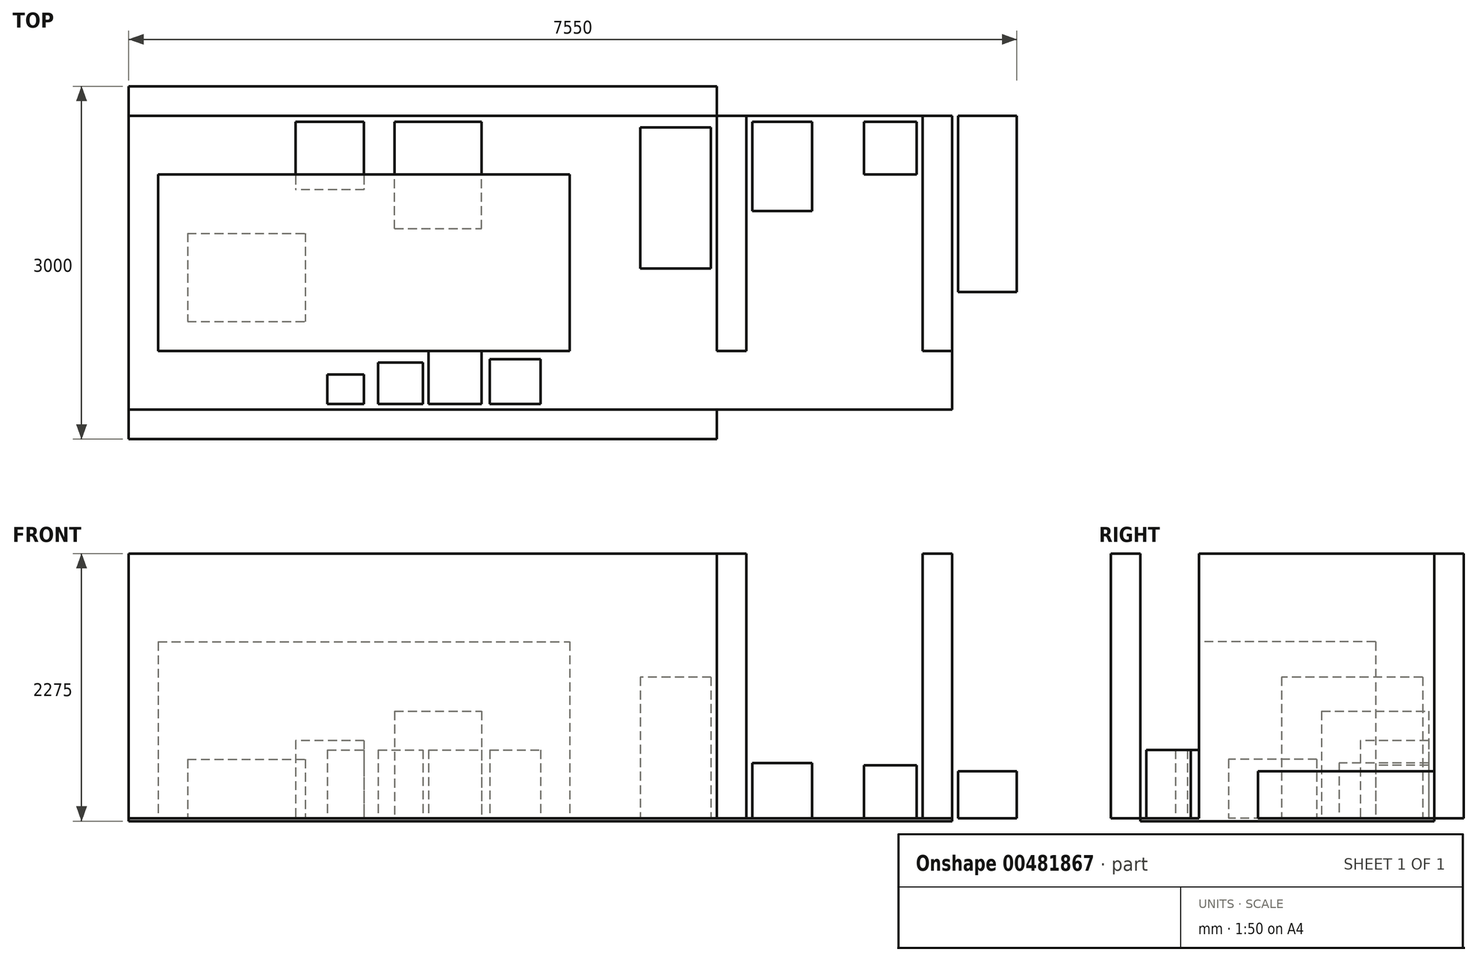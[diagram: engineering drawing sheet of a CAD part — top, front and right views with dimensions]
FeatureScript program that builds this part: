
annotation { "Feature Type Name" : "Feature", "Feature Type Description" : "" }
export const myFeature = defineFeature(function(context is Context, id is Id, definition is map)
    precondition{}
    {
        {
            var Q0;
            Q0=qCreatedBy(makeId("Top.planeOp"),FACE);
            var sketch = newSketch(context, id + "F0", { "sketchPlane" : qUnion([Q0])});
            skLineSegment(sketch, "E0.bottom", {"start": v(-2500, -1250) * mm, "end": v(2500, -1250) * mm});
            skLineSegment(sketch, "E0.top", {"start": v(-2500, 1250) * mm, "end": v(2500, 1250) * mm});
            skLineSegment(sketch, "E0.left", {"start": v(-2500, -1250) * mm, "end": v(-2500, 1250) * mm});
            skLineSegment(sketch, "E0.right", {"start": v(2500, -1250) * mm, "end": v(2500, 1250) * mm});
            skPoint(sketch, "E0.middle", {"position": v(0, 0) * mm});
            skSolve(sketch);
        }
        {
            var Q0;
            Q0=makeQuery(id+"F0.imprint","IMPRINT",FACE,{"disambiguationData":[TD([[makeQuery(id+"F0.imprint","IMPRINT",EDGE,{"derivedFrom":sQuery(id+"F0.wireOp",EDGE,"E0.bottom")}),1.0]])]});
            extrude(context, id + "F1", {"entities" : qUnion([Q0]), "depth" : 25 * mm});
        }
        {
            var Q0;
            Q0=qCreatedBy(makeId("Top.planeOp"),FACE);
            var sketch = newSketch(context, id + "F2", { "sketchPlane" : qUnion([Q0])});
            skLineSegment(sketch, "E1.bottom", {"start": v(2500, -1250) * mm, "end": v(4500, -1250) * mm});
            skLineSegment(sketch, "E1.top", {"start": v(2500, 1250) * mm, "end": v(4500, 1250) * mm});
            skLineSegment(sketch, "E1.left", {"start": v(2500, -1250) * mm, "end": v(2500, 1250) * mm});
            skLineSegment(sketch, "E1.right", {"start": v(4500, -1250) * mm, "end": v(4500, 1250) * mm});
            skSolve(sketch);
        }
        {
            var Q0;
            Q0=makeQuery(id+"F2.imprint","IMPRINT",FACE,{"disambiguationData":[TD([[makeQuery(id+"F2.imprint","IMPRINT",EDGE,{"derivedFrom":sQuery(id+"F2.wireOp",EDGE,"E1.bottom")}),1.0]])]});
            extrude(context, id + "F3", {"entities" : qUnion([Q0]), "depth" : 25 * mm});
        }
        {
            var Q0;
            Q0=makeQuery(id+"F1.opExtrude","CAP_FACE",FACE,{"disambiguationData":[OSD([sQuery(id+"F0.wireOp",EDGE,"E0.bottom"),sQuery(id+"F0.wireOp",EDGE,"E0.top"),sQuery(id+"F0.wireOp",EDGE,"E0.left"),sQuery(id+"F0.wireOp",EDGE,"E0.right")])],"isStart":false});
            var sketch = newSketch(context, id + "F4", { "sketchPlane" : qUnion([Q0])});
            skLineSegment(sketch, "E2.bottom", {"start": v(-2500, -1250) * mm, "end": v(2500, -1250) * mm});
            skLineSegment(sketch, "E2.top", {"start": v(-2500, -1500) * mm, "end": v(2500, -1500) * mm});
            skLineSegment(sketch, "E2.left", {"start": v(-2500, -1250) * mm, "end": v(-2500, -1500) * mm});
            skLineSegment(sketch, "E2.right", {"start": v(2500, -1250) * mm, "end": v(2500, -1500) * mm});
            skLineSegment(sketch, "E3.bottom", {"start": v(-2500, 1250) * mm, "end": v(2500, 1250) * mm});
            skLineSegment(sketch, "E3.top", {"start": v(-2500, 1500) * mm, "end": v(2500, 1500) * mm});
            skLineSegment(sketch, "E3.left", {"start": v(-2500, 1250) * mm, "end": v(-2500, 1500) * mm});
            skLineSegment(sketch, "E3.right", {"start": v(2500, 1250) * mm, "end": v(2500, 1500) * mm});
            skLineSegment(sketch, "E4.bottom", {"start": v(2500, 1250) * mm, "end": v(2750, 1250) * mm});
            skLineSegment(sketch, "E4.top", {"start": v(2500, -750) * mm, "end": v(2750, -750) * mm});
            skLineSegment(sketch, "E4.left", {"start": v(2500, 1250) * mm, "end": v(2500, -750) * mm});
            skLineSegment(sketch, "E4.right", {"start": v(2750, 1250) * mm, "end": v(2750, -750) * mm});
            skLineSegment(sketch, "E5.bottom", {"start": v(4500, 1250) * mm, "end": v(4250, 1250) * mm});
            skLineSegment(sketch, "E5.top", {"start": v(4500, -750) * mm, "end": v(4250, -750) * mm});
            skLineSegment(sketch, "E5.left", {"start": v(4500, 1250) * mm, "end": v(4500, -750) * mm});
            skLineSegment(sketch, "E5.right", {"start": v(4250, 1250) * mm, "end": v(4250, -750) * mm});
            skSolve(sketch);
        }
        {
            var Q0;
            Q0 = qSketchRegion(id + "F4", true);
            extrude(context, id + "F5", {"entities" : qUnion([Q0]), "operationType" : NewBodyOperationType.ADD, "depth" : 2250 * mm});
        }
        {
            var Q0;
            Q0=makeQuery(id+"F1.opExtrude","CAP_FACE",FACE,{"disambiguationData":[OSD([sQuery(id+"F0.wireOp",EDGE,"E0.bottom"),sQuery(id+"F0.wireOp",EDGE,"E0.top"),sQuery(id+"F0.wireOp",EDGE,"E0.left"),sQuery(id+"F0.wireOp",EDGE,"E0.right")])],"isStart":false});
            var sketch = newSketch(context, id + "F6", { "sketchPlane" : qUnion([Q0])});
            skLineSegment(sketch, "E6.bottom", {"start": v(-2250, 750) * mm, "end": v(1250, 750) * mm});
            skLineSegment(sketch, "E6.top", {"start": v(-2250, -750) * mm, "end": v(1250, -750) * mm});
            skLineSegment(sketch, "E6.left", {"start": v(-2250, 750) * mm, "end": v(-2250, -750) * mm});
            skLineSegment(sketch, "E6.right", {"start": v(1250, 750) * mm, "end": v(1250, -750) * mm});
            skPoint(sketch, "E6.middle", {"position": v(-500, 0) * mm});
            skSolve(sketch);
        }
        {
            var Q0;
            Q0 = qSketchRegion(id + "F6", true);
            extrude(context, id + "F7", {"entities" : qUnion([Q0]), "depth" : 1500 * mm});
        }
        {
            var Q0;
            Q0=makeQuery(id+"F1.opExtrude","CAP_FACE",FACE,{"disambiguationData":[OSD([sQuery(id+"F0.wireOp",EDGE,"E0.bottom"),sQuery(id+"F0.wireOp",EDGE,"E0.top"),sQuery(id+"F0.wireOp",EDGE,"E0.left"),sQuery(id+"F0.wireOp",EDGE,"E0.right")])],"isStart":false});
            var sketch = newSketch(context, id + "F8", { "sketchPlane" : qUnion([Q0])});
            skLineSegment(sketch, "E7.bottom", {"start": v(-240, 290) * mm, "end": v(500, 290) * mm});
            skLineSegment(sketch, "E7.top", {"start": v(-240, 1200) * mm, "end": v(500, 1200) * mm});
            skLineSegment(sketch, "E7.left", {"start": v(-240, 290) * mm, "end": v(-240, 1200) * mm});
            skLineSegment(sketch, "E7.right", {"start": v(500, 290) * mm, "end": v(500, 1200) * mm});
            skSolve(sketch);
        }
        {
            var Q0;
            Q0 = qSketchRegion(id + "F8", true);
            extrude(context, id + "F9", {"entities" : qUnion([Q0]), "depth" : 910 * mm});
        }
        {
            var Q0;
            Q0=makeQuery(id+"F1.opExtrude","CAP_FACE",FACE,{"disambiguationData":[OSD([sQuery(id+"F0.wireOp",EDGE,"E0.bottom"),sQuery(id+"F0.wireOp",EDGE,"E0.top"),sQuery(id+"F0.wireOp",EDGE,"E0.left"),sQuery(id+"F0.wireOp",EDGE,"E0.right")])],"isStart":false});
            var sketch = newSketch(context, id + "F10", { "sketchPlane" : qUnion([Q0])});
            skLineSegment(sketch, "E8.bottom", {"start": v(2450, 1150) * mm, "end": v(1850, 1150) * mm});
            skLineSegment(sketch, "E8.top", {"start": v(2450, -50) * mm, "end": v(1850, -50) * mm});
            skLineSegment(sketch, "E8.left", {"start": v(2450, 1150) * mm, "end": v(2450, -50) * mm});
            skLineSegment(sketch, "E8.right", {"start": v(1850, 1150) * mm, "end": v(1850, -50) * mm});
            skSolve(sketch);
        }
        {
            var Q0;
            Q0 = qSketchRegion(id + "F10", true);
            extrude(context, id + "F11", {"entities" : qUnion([Q0]), "depth" : 1200 * mm});
        }
        {
            var Q0;
            Q0=makeQuery(id+"F1.opExtrude","CAP_FACE",FACE,{"disambiguationData":[OSD([sQuery(id+"F0.wireOp",EDGE,"E0.bottom"),sQuery(id+"F0.wireOp",EDGE,"E0.top"),sQuery(id+"F0.wireOp",EDGE,"E0.left"),sQuery(id+"F0.wireOp",EDGE,"E0.right")])],"isStart":false});
            var sketch = newSketch(context, id + "F12", { "sketchPlane" : qUnion([Q0])});
            skLineSegment(sketch, "E9.bottom", {"start": v(-500, 1200) * mm, "end": v(-1080, 1200) * mm});
            skLineSegment(sketch, "E9.top", {"start": v(-500, 620) * mm, "end": v(-1080, 620) * mm});
            skLineSegment(sketch, "E9.left", {"start": v(-500, 1200) * mm, "end": v(-500, 620) * mm});
            skLineSegment(sketch, "E9.right", {"start": v(-1080, 1200) * mm, "end": v(-1080, 620) * mm});
            skSolve(sketch);
        }
        {
            var Q0;
            Q0 = qSketchRegion(id + "F12", true);
            extrude(context, id + "F13", {"entities" : qUnion([Q0]), "depth" : 660 * mm});
        }
        {
            var Q0;
            Q0=makeQuery(id+"F3.opExtrude","CAP_FACE",FACE,{"disambiguationData":[OSD([sQuery(id+"F2.wireOp",EDGE,"E1.bottom"),sQuery(id+"F2.wireOp",EDGE,"E1.top"),sQuery(id+"F2.wireOp",EDGE,"E1.left"),sQuery(id+"F2.wireOp",EDGE,"E1.right")])],"isStart":false});
            var sketch = newSketch(context, id + "F14", { "sketchPlane" : qUnion([Q0])});
            skLineSegment(sketch, "E10.bottom", {"start": v(4550, 1250) * mm, "end": v(5050, 1250) * mm});
            skLineSegment(sketch, "E10.top", {"start": v(4550, -250) * mm, "end": v(5050, -250) * mm});
            skLineSegment(sketch, "E10.left", {"start": v(4550, 1250) * mm, "end": v(4550, -250) * mm});
            skLineSegment(sketch, "E10.right", {"start": v(5050, 1250) * mm, "end": v(5050, -250) * mm});
            skSolve(sketch);
        }
        {
            var Q0;
            Q0=makeQuery(id+"F14.imprint","IMPRINT",FACE,{"disambiguationData":[TD([[makeQuery(id+"F14.imprint","IMPRINT",EDGE,{"derivedFrom":sQuery(id+"F14.wireOp",EDGE,"E10.bottom")}),-1.0]])]});
            extrude(context, id + "F15", {"entities" : qUnion([Q0]), "depth" : 400 * mm});
        }
        {
            var Q0;
            Q0=makeQuery(id+"F3.opExtrude","CAP_FACE",FACE,{"disambiguationData":[OSD([sQuery(id+"F2.wireOp",EDGE,"E1.bottom"),sQuery(id+"F2.wireOp",EDGE,"E1.top"),sQuery(id+"F2.wireOp",EDGE,"E1.left"),sQuery(id+"F2.wireOp",EDGE,"E1.right")])],"isStart":false});
            var sketch = newSketch(context, id + "F16", { "sketchPlane" : qUnion([Q0])});
            skLineSegment(sketch, "E11.bottom", {"start": v(2800, 1200) * mm, "end": v(3310, 1200) * mm});
            skLineSegment(sketch, "E11.top", {"start": v(2800, 440) * mm, "end": v(3310, 440) * mm});
            skLineSegment(sketch, "E11.left", {"start": v(2800, 1200) * mm, "end": v(2800, 440) * mm});
            skLineSegment(sketch, "E11.right", {"start": v(3310, 1200) * mm, "end": v(3310, 440) * mm});
            skSolve(sketch);
        }
        {
            var Q0;
            Q0=makeQuery(id+"F16.imprint","IMPRINT",FACE,{"disambiguationData":[TD([[makeQuery(id+"F16.imprint","IMPRINT",EDGE,{"derivedFrom":sQuery(id+"F16.wireOp",EDGE,"E11.bottom")}),-1.0]])]});
            extrude(context, id + "F17", {"entities" : qUnion([Q0]), "depth" : 470 * mm});
        }
        {
            var Q0;
            Q0=makeQuery(id+"F3.opExtrude","CAP_FACE",FACE,{"disambiguationData":[OSD([sQuery(id+"F2.wireOp",EDGE,"E1.bottom"),sQuery(id+"F2.wireOp",EDGE,"E1.top"),sQuery(id+"F2.wireOp",EDGE,"E1.left"),sQuery(id+"F2.wireOp",EDGE,"E1.right")])],"isStart":false});
            var sketch = newSketch(context, id + "F18", { "sketchPlane" : qUnion([Q0])});
            skLineSegment(sketch, "E12.bottom", {"start": v(4200, 1200) * mm, "end": v(3750, 1200) * mm});
            skLineSegment(sketch, "E12.top", {"start": v(4200, 750) * mm, "end": v(3750, 750) * mm});
            skLineSegment(sketch, "E12.left", {"start": v(4200, 1200) * mm, "end": v(4200, 750) * mm});
            skLineSegment(sketch, "E12.right", {"start": v(3750, 1200) * mm, "end": v(3750, 750) * mm});
            skPoint(sketch, "E12.middle", {"position": v(3975, 975) * mm});
            skSolve(sketch);
        }
        {
            var Q0;
            Q0 = qSketchRegion(id + "F18", true);
            extrude(context, id + "F19", {"entities" : qUnion([Q0]), "depth" : 450 * mm});
        }
        {
            var Q0;
            Q0=makeQuery(id+"F1.opExtrude","CAP_FACE",FACE,{"disambiguationData":[OSD([sQuery(id+"F0.wireOp",EDGE,"E0.bottom"),sQuery(id+"F0.wireOp",EDGE,"E0.top"),sQuery(id+"F0.wireOp",EDGE,"E0.left"),sQuery(id+"F0.wireOp",EDGE,"E0.right")])],"isStart":false});
            var sketch = newSketch(context, id + "F20", { "sketchPlane" : qUnion([Q0])});
            skLineSegment(sketch, "E13.bottom", {"start": v(-380, -850) * mm, "end": v(0, -850) * mm});
            skLineSegment(sketch, "E13.top", {"start": v(-380, -1200) * mm, "end": v(0, -1200) * mm});
            skLineSegment(sketch, "E13.left", {"start": v(-380, -850) * mm, "end": v(-380, -1200) * mm});
            skLineSegment(sketch, "E13.right", {"start": v(0, -850) * mm, "end": v(0, -1200) * mm});
            skLineSegment(sketch, "E14.bottom", {"start": v(-810, -950) * mm, "end": v(-500, -950) * mm});
            skLineSegment(sketch, "E14.top", {"start": v(-810, -1200) * mm, "end": v(-500, -1200) * mm});
            skLineSegment(sketch, "E14.left", {"start": v(-810, -950) * mm, "end": v(-810, -1200) * mm});
            skLineSegment(sketch, "E14.right", {"start": v(-500, -950) * mm, "end": v(-500, -1200) * mm});
            skLineSegment(sketch, "E15.bottom", {"start": v(50, -750) * mm, "end": v(500, -750) * mm});
            skLineSegment(sketch, "E15.top", {"start": v(50, -1200) * mm, "end": v(500, -1200) * mm});
            skLineSegment(sketch, "E15.left", {"start": v(50, -750) * mm, "end": v(50, -1200) * mm});
            skLineSegment(sketch, "E15.right", {"start": v(500, -750) * mm, "end": v(500, -1200) * mm});
            skLineSegment(sketch, "E16.bottom", {"start": v(570, -820) * mm, "end": v(1000, -820) * mm});
            skLineSegment(sketch, "E16.top", {"start": v(570, -1200) * mm, "end": v(1000, -1200) * mm});
            skLineSegment(sketch, "E16.left", {"start": v(570, -820) * mm, "end": v(570, -1200) * mm});
            skLineSegment(sketch, "E16.right", {"start": v(1000, -820) * mm, "end": v(1000, -1200) * mm});
            skSolve(sketch);
        }
        {
            var Q0;
            Q0 = qSketchRegion(id + "F20", true);
            extrude(context, id + "F21", {"entities" : qUnion([Q0]), "depth" : 580 * mm});
        }
        {
            var Q0;
            Q0=makeQuery(id+"F1.opExtrude","CAP_FACE",FACE,{"disambiguationData":[OSD([sQuery(id+"F0.wireOp",EDGE,"E0.bottom"),sQuery(id+"F0.wireOp",EDGE,"E0.top"),sQuery(id+"F0.wireOp",EDGE,"E0.left"),sQuery(id+"F0.wireOp",EDGE,"E0.right")])],"isStart":false});
            var sketch = newSketch(context, id + "F22", { "sketchPlane" : qUnion([Q0])});
            skLineSegment(sketch, "E17.bottom", {"start": v(-2000, 250) * mm, "end": v(-1000, 250) * mm});
            skLineSegment(sketch, "E17.top", {"start": v(-2000, -500) * mm, "end": v(-1000, -500) * mm});
            skLineSegment(sketch, "E17.left", {"start": v(-2000, 250) * mm, "end": v(-2000, -500) * mm});
            skLineSegment(sketch, "E17.right", {"start": v(-1000, 250) * mm, "end": v(-1000, -500) * mm});
            skSolve(sketch);
        }
        {
            var Q0;
            Q0 = qSketchRegion(id + "F22", true);
            extrude(context, id + "F23", {"entities" : qUnion([Q0]), "depth" : 500 * mm});
        }
    });
